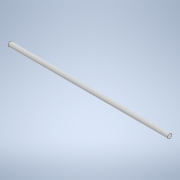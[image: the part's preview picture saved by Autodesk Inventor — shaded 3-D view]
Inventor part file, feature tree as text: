
AUTODESK INVENTOR PART (.ipt)
format: ipt  version: 2021 (Build 250183000, 183)  size: 97,280 bytes
history: native  units: mm
features: revolve x1, sketch x1
ambient origin geometry x8: Origin, YZ Plane, XZ Plane, XY Plane, X Axis, Y Axis, Z Axis, Center Point
bodies: Solid1 (feature_tree)
feature tree (2):
  revolve  "Revolution1"  [1 undecoded]
  sketch  "Sketch1"  dims[d0=3.3mm d1=240.0mm d2=90.0deg]
note: 1 required parameter value undecoded (feature->parameter linkage not recoverable at this tier; creation-order binding heuristic only, values carry confidence <= 0.55)
